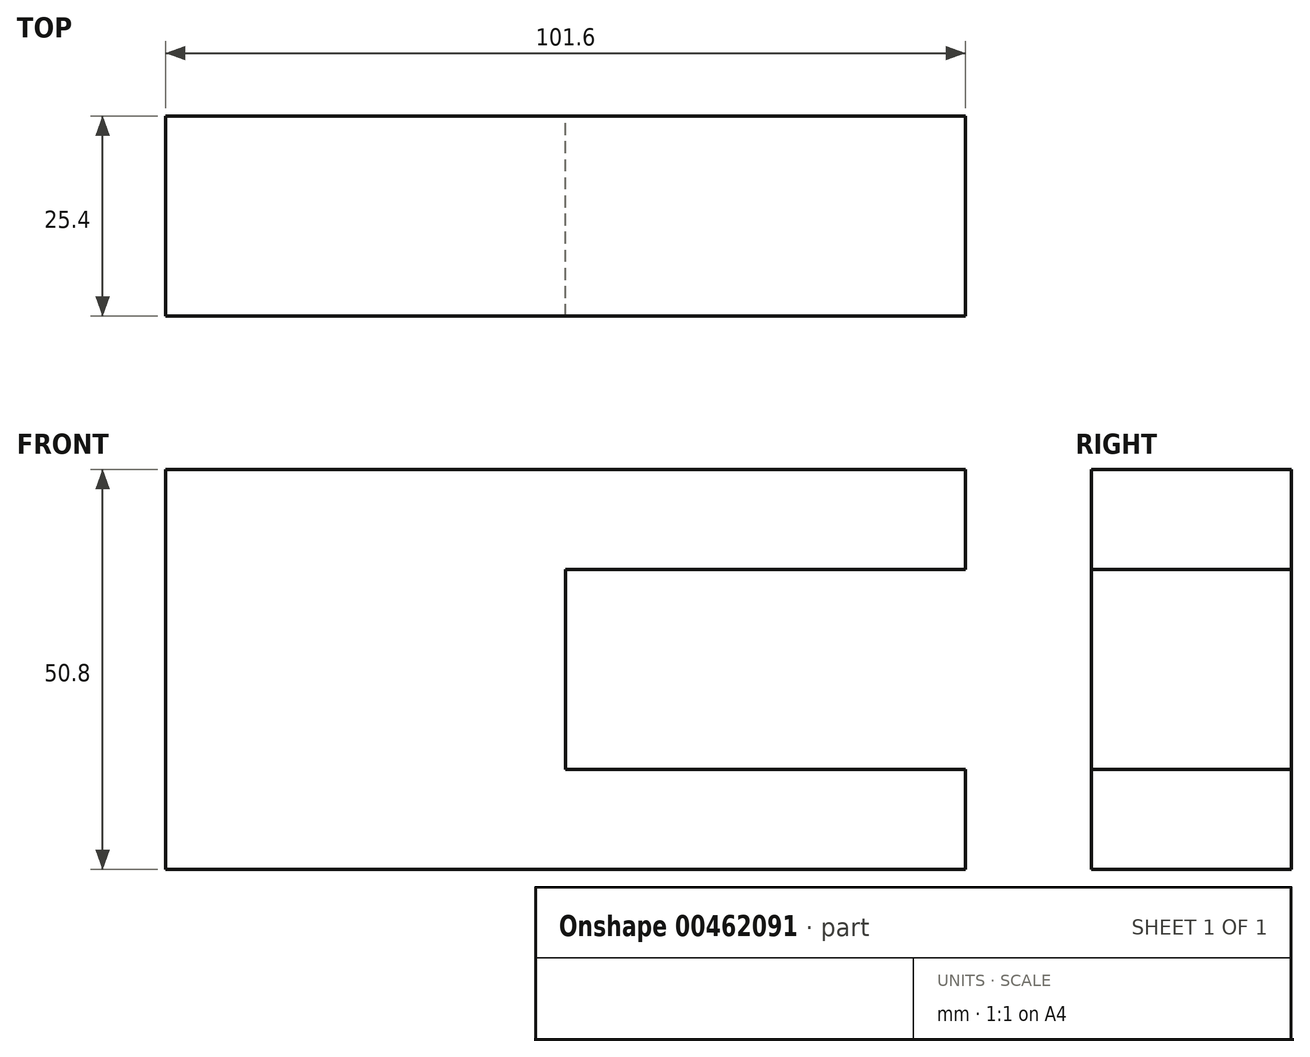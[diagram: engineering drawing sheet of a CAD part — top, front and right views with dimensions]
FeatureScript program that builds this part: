
annotation { "Feature Type Name" : "Feature", "Feature Type Description" : "" }
export const myFeature = defineFeature(function(context is Context, id is Id, definition is map)
    precondition{}
    {
        {
            var Q0;
            Q0=qCreatedBy(makeId("Front.planeOp"),FACE);
            var sketch = newSketch(context, id + "F0", { "sketchPlane" : qUnion([Q0])});
            skLineSegment(sketch, "E0.bottom", {"start": v(-50.8, 25.4) * mm, "end": v(50.8, 25.4) * mm});
            skLineSegment(sketch, "E0.top", {"start": v(-50.8, -25.4) * mm, "end": v(50.8, -25.4) * mm});
            skLineSegment(sketch, "E0.left", {"start": v(-50.8, 25.4) * mm, "end": v(-50.8, -25.4) * mm});
            skLineSegment(sketch, "E0.right", {"start": v(50.8, 25.4) * mm, "end": v(50.8, -25.4) * mm});
            skPoint(sketch, "E0.middle", {"position": v(0, 0) * mm});
            skSolve(sketch);
        }
        {
            var Q0;
            Q0=qSketchRegion(id+"F0",true);
            extrude(context, id + "F1", {"entities" : qUnion([Q0]), "depth" : 25.4 * mm});
        }
        {
            var Q0;
            Q0=qCreatedBy(makeId("Front.planeOp"),FACE);
            var sketch = newSketch(context, id + "F2", { "sketchPlane" : qUnion([Q0])});
            skLineSegment(sketch, "E1.bottom", {"start": v(50.8, -12.7) * mm, "end": v(0, -12.7) * mm});
            skLineSegment(sketch, "E1.top", {"start": v(50.8, 12.7) * mm, "end": v(0, 12.7) * mm});
            skLineSegment(sketch, "E1.left", {"start": v(50.8, -12.7) * mm, "end": v(50.8, 12.7) * mm});
            skLineSegment(sketch, "E1.right", {"start": v(0, -12.7) * mm, "end": v(0, 12.7) * mm});
            skSolve(sketch);
        }
        {
            var Q0;
            Q0=qSketchRegion(id+"F2",true);
            extrude(context, id + "F3", {"entities" : qUnion([Q0]), "operationType" : NewBodyOperationType.REMOVE, "endBound" : BoundingType.THROUGH_ALL, "oppositeDirection" : true, "depth" : 25.4 * mm});
        }
        {
            var Q0;
            Q0=makeQuery(id+"F2.imprint","IMPRINT",FACE,{"disambiguationData":[TD([[makeQuery(id+"F2.imprint","IMPRINT",EDGE,{"derivedFrom":sQuery(id+"F2.wireOp",EDGE,"E1.bottom")}),-1.0]])]});
            extrude(context, id + "F4", {"entities" : qUnion([Q0]), "operationType" : NewBodyOperationType.REMOVE, "endBound" : BoundingType.THROUGH_ALL, "depth" : 25.4 * mm});
        }
    });
